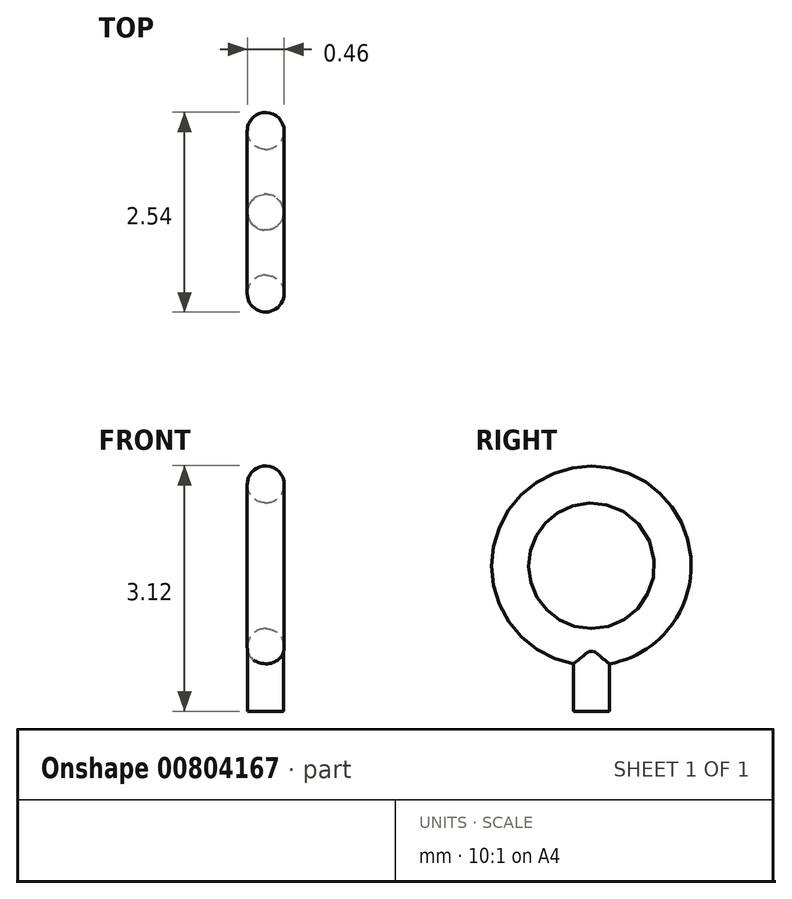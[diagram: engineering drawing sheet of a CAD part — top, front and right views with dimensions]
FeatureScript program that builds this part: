
annotation { "Feature Type Name" : "Feature", "Feature Type Description" : "" }
export const myFeature = defineFeature(function(context is Context, id is Id, definition is map)
    precondition{}
    {
        {
            var Q0;
            Q0=qCreatedBy(makeId("Top.planeOp"),FACE);
            var sketch = newSketch(context, id + "F0", { "sketchPlane" : qUnion([Q0])});
            skCircle(sketch, "E0", {"center": v(0, 0) * mm, "radius": 3.17 * mm});
            skSolve(sketch);
        }
        {
            var Q0;
            Q0 = qSketchRegion(id + "F0", true);
            extrude(context, id + "F1", {"entities" : qUnion([Q0]), "depth" : 152.4 * mm, "offsetDistance" : 25.4 * mm});
        }
        {
            var Q0;
            Q0=makeQuery(id+"F1.opExtrude","SWEPT_BODY",BODY,{"disambiguationData":[OSD([sQuery(id+"F0.wireOp",EDGE,"E0")])]});
            deleteBodies(context, id + "F2", {"entities" : qUnion([Q0])});
        }
        {
            var Q0;
            Q0=qCreatedBy(makeId("Top.planeOp"),FACE);
            var sketch = newSketch(context, id + "F3", { "sketchPlane" : qUnion([Q0])});
            skCircle(sketch, "E1", {"center": v(0, 0) * mm, "radius": 0.23 * mm});
            skSolve(sketch);
        }
        {
            var Q0;
            Q0 = qSketchRegion(id + "F3", true);
            extrude(context, id + "F4", {"entities" : qUnion([Q0]), "depth" : 0.81 * mm, "offsetDistance" : 25.4 * mm});
        }
        {
            var Q0;
            Q0=qCreatedBy(makeId("Right.planeOp"),FACE);
            var sketch = newSketch(context, id + "F5", { "sketchPlane" : qUnion([Q0])});
            skCircle(sketch, "E2", {"center": v(0, 1.85) * mm, "radius": 1.14 * mm});
            skSolve(sketch);
        }
        {
            var Q0;
            Q0=qCreatedBy(makeId("Front.planeOp"),FACE);
            var sketch = newSketch(context, id + "F6", { "sketchPlane" : qUnion([Q0])});
            skCircle(sketch, "E3", {"center": v(0, 0.82) * mm, "radius": 0.23 * mm});
            skSolve(sketch);
        }
        {
            var Q0;
            Q0=makeQuery(id+"F6.imprint","IMPRINT",FACE,{"disambiguationData":[TD([[makeQuery(id+"F6.imprint","IMPRINT",EDGE,{"derivedFrom":sQuery(id+"F6.wireOp",EDGE,"E3")}),1.0]])]});
            var Q1;
            Q1=sQuery(id+"F5.wireOp",EDGE,"E2");
            revolve(context, id + "F7", {"operationType" : NewBodyOperationType.ADD, "surfaceOperationType" : NewSurfaceOperationType.NEW, "entities" : qUnion([Q0]), "axis" : qUnion([Q1]), "revolveType" : RevolveType.FULL});
        }
    });
